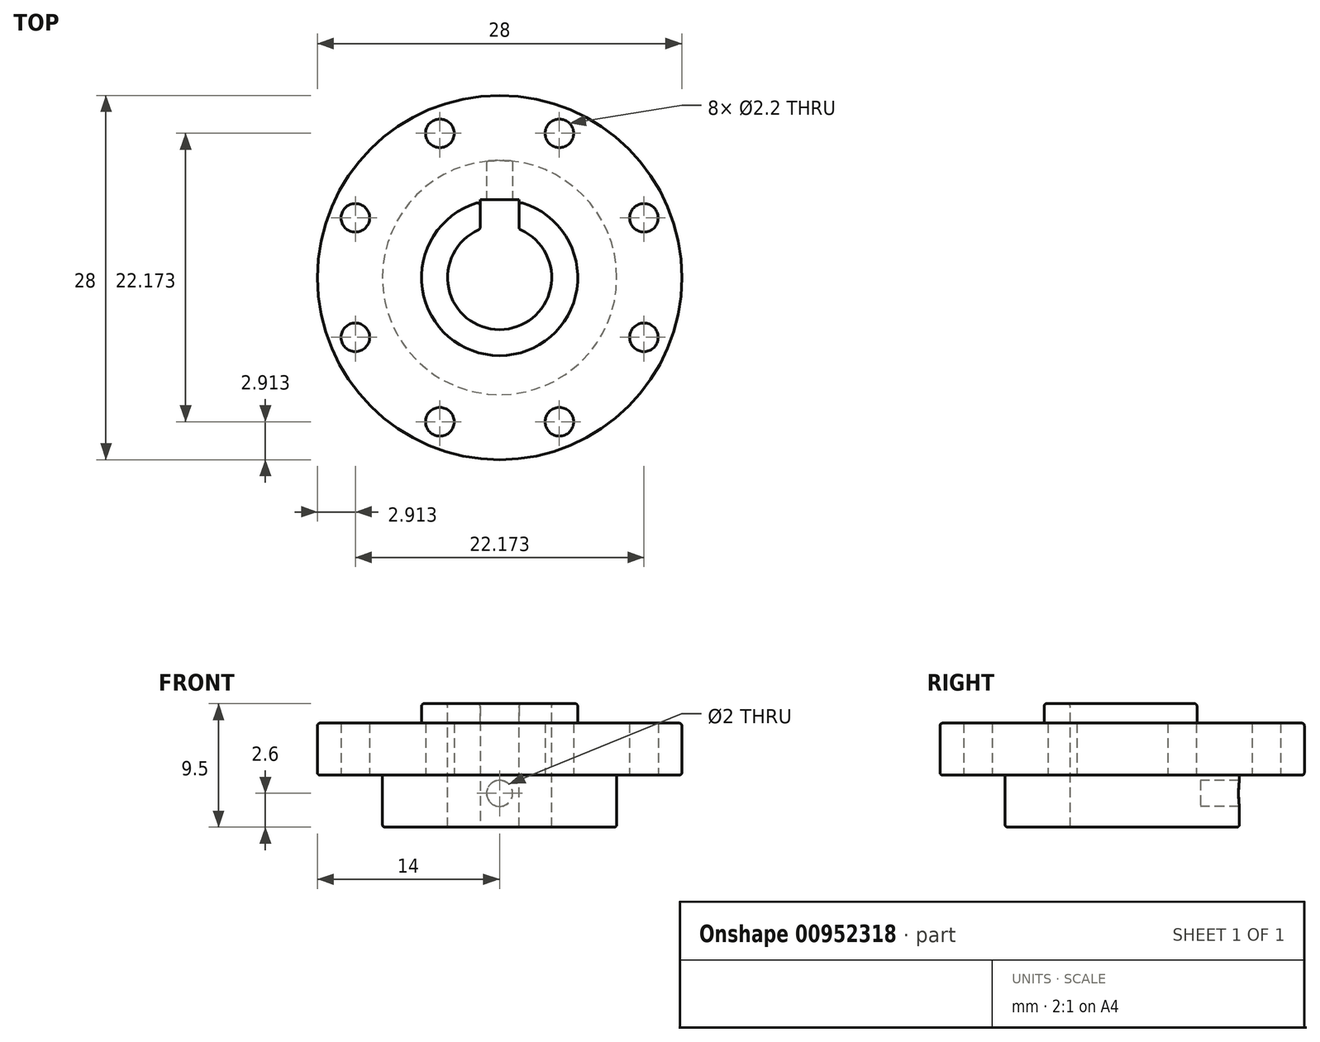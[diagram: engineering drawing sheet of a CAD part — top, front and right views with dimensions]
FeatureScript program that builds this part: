
annotation { "Feature Type Name" : "Feature", "Feature Type Description" : "" }
export const myFeature = defineFeature(function(context is Context, id is Id, definition is map)
    precondition{}
    {
        {
            var Q0;
            Q0=qCreatedBy(makeId("Top.planeOp"),FACE);
            var sketch = newSketch(context, id + "F0", { "sketchPlane" : qUnion([Q0])});
            skCircle(sketch, "E0", {"center": v(0, 0) * mm, "radius": 14 * mm});
            skSolve(sketch);
        }
        {
            var Q0;
            Q0 = qSketchRegion(id + "F0", true);
            extrude(context, id + "F1", {"entities" : qUnion([Q0]), "depth" : 4 * mm, "offsetDistance" : 25 * mm});
        }
        {
            var Q0;
            Q0=makeQuery(id+"F1.opExtrude","CAP_FACE",FACE,{"disambiguationData":[OSD([sQuery(id+"F0.wireOp",EDGE,"knUi2pX4-qsrH-ZYnk-r2x0-8cSF1UmVhSbS"),sQuery(id+"F0.wireOp",EDGE,"E0")])],"isStart":true});
            var sketch = newSketch(context, id + "F2", { "sketchPlane" : qUnion([Q0])});
            skCircle(sketch, "E1", {"center": v(0, 0) * mm, "radius": 9 * mm});
            skSolve(sketch);
        }
        {
            var Q0;
            Q0 = qSketchRegion(id + "F2", true);
            extrude(context, id + "F3", {"entities" : qUnion([Q0]), "operationType" : NewBodyOperationType.ADD, "depth" : 4 * mm, "offsetDistance" : 25 * mm});
        }
        {
            var Q0;
            Q0=makeQuery(id+"F1.opExtrude","CAP_FACE",FACE,{"disambiguationData":[OSD([sQuery(id+"F0.wireOp",EDGE,"E0")])],"isStart":false});
            var sketch = newSketch(context, id + "F4", { "sketchPlane" : qUnion([Q0])});
            skCircle(sketch, "E2", {"center": v(0, 0) * mm, "radius": 4 * mm});
            skSolve(sketch);
        }
        {
            var Q0;
            Q0 = qSketchRegion(id + "F4", true);
            var Q1;
            Q1=makeQuery(id+"F3.opExtrude","CAP_FACE",FACE,{"disambiguationData":[OSD([sQuery(id+"F2.wireOp",EDGE,"E1")])],"isStart":false});
            extrude(context, id + "F5", {"entities" : qUnion([Q0]), "operationType" : NewBodyOperationType.REMOVE, "endBound" : BoundingType.UP_TO_SURFACE, "oppositeDirection" : true, "depth" : 25 * mm, "endBoundEntityFace" : qUnion([Q1]), "offsetDistance" : 25 * mm});
        }
        {
            var Q0;
            Q0=makeQuery(id+"F1.opExtrude","CAP_FACE",FACE,{"disambiguationData":[OSD([sQuery(id+"F0.wireOp",EDGE,"E0")])],"isStart":true});
            var sketch = newSketch(context, id + "F6", { "sketchPlane" : qUnion([Q0])});
            skCircle(sketch, "E3", {"center": v(4.6, 11.09) * mm, "radius": 1.1 * mm});
            skCircle(sketch, "E4.1.0", {"center": v(-4.6, 11.09) * mm, "radius": 1.1 * mm});
            skCircle(sketch, "E4.2.0", {"center": v(-11.09, 4.6) * mm, "radius": 1.1 * mm});
            skCircle(sketch, "E4.3.0", {"center": v(-11.09, -4.6) * mm, "radius": 1.1 * mm});
            skCircle(sketch, "E4.4.0", {"center": v(-4.6, -11.09) * mm, "radius": 1.1 * mm});
            skCircle(sketch, "E4.5.0", {"center": v(4.6, -11.09) * mm, "radius": 1.1 * mm});
            skCircle(sketch, "E4.6.0", {"center": v(11.09, -4.6) * mm, "radius": 1.1 * mm});
            skCircle(sketch, "E4.7.0", {"center": v(11.09, 4.6) * mm, "radius": 1.1 * mm});
            skPoint(sketch, "E4.center", {"position": v(0, 0) * mm});
            skLineSegment(sketch, "E5", {"start": v(4.6, -11.09) * mm, "end": v(0, 0) * mm});
            skSolve(sketch);
        }
        {
            var Q0;
            Q0 = qSketchRegion(id + "F6", true);
            var Q1;
            Q1=makeQuery(id+"F1.opExtrude","CAP_FACE",FACE,{"disambiguationData":[OSD([sQuery(id+"F0.wireOp",EDGE,"E0")])],"isStart":false});
            extrude(context, id + "F7", {"entities" : qUnion([Q0]), "operationType" : NewBodyOperationType.REMOVE, "endBound" : BoundingType.UP_TO_SURFACE, "oppositeDirection" : true, "depth" : 25 * mm, "endBoundEntityFace" : qUnion([Q1]), "offsetDistance" : 25 * mm});
        }
        {
            var Q0;
            Q0=makeQuery(id+"F1.opExtrude","CAP_FACE",FACE,{"disambiguationData":[OSD([sQuery(id+"F0.wireOp",EDGE,"E0")])],"isStart":false});
            var sketch = newSketch(context, id + "F8", { "sketchPlane" : qUnion([Q0])});
            skLineSegment(sketch, "E6.bottom", {"start": v(1.5, 3) * mm, "end": v(-1.5, 3) * mm});
            skLineSegment(sketch, "E6.top", {"start": v(1.5, 6) * mm, "end": v(-1.5, 6) * mm});
            skLineSegment(sketch, "E6.left", {"start": v(1.5, 3) * mm, "end": v(1.5, 6) * mm});
            skLineSegment(sketch, "E6.right", {"start": v(-1.5, 3) * mm, "end": v(-1.5, 6) * mm});
            skPoint(sketch, "E6.middle", {"position": v(0, 4.5) * mm});
            skSolve(sketch);
        }
        {
            var Q0;
            {var subQ0=sQuery(id+"F8.wireOp",EDGE,"E6.top");Q0=makeQuery(id+"F8.imprint","IMPRINT",FACE,{"disambiguationData":[TD([[makeQuery(id+"F8.imprint","IMPRINT",EDGE,{"derivedFrom":subQ0}),1.0]])]});}
            var Q1;
            Q1=makeQuery(id+"F3.opExtrude","CAP_FACE",FACE,{"disambiguationData":[OSD([sQuery(id+"F2.wireOp",EDGE,"E1")])],"isStart":false});
            extrude(context, id + "F9", {"entities" : qUnion([Q0]), "operationType" : NewBodyOperationType.REMOVE, "endBound" : BoundingType.UP_TO_SURFACE, "oppositeDirection" : true, "depth" : 25 * mm, "endBoundEntityFace" : qUnion([Q1]), "offsetDistance" : 25 * mm});
        }
        {
            var Q0;
            Q0=qCreatedBy(makeId("Front.planeOp"),FACE);
            var sketch = newSketch(context, id + "F10", { "sketchPlane" : qUnion([Q0])});
            skCircle(sketch, "E7", {"center": v(0, -1.4) * mm, "radius": 1 * mm});
            skSolve(sketch);
        }
        {
            var Q0;
            Q0 = qSketchRegion(id + "F10", true);
            extrude(context, id + "F11", {"entities" : qUnion([Q0]), "operationType" : NewBodyOperationType.REMOVE, "oppositeDirection" : true, "depth" : 25 * mm, "offsetDistance" : 25 * mm});
        }
        {
            var Q0;
            Q0=makeQuery(id+"F1.opExtrude","CAP_FACE",FACE,{"disambiguationData":[OSD([sQuery(id+"F0.wireOp",EDGE,"E0")])],"isStart":false});
            var sketch = newSketch(context, id + "F12", { "sketchPlane" : qUnion([Q0])});
            skCircle(sketch, "E8", {"center": v(0, 0) * mm, "radius": 6 * mm});
            skCircle(sketch, "E9", {"center": v(0, 0) * mm, "radius": 4 * mm});
            skLineSegment(sketch, "E10", {"start": v(-1.5, 3.7) * mm, "end": v(-1.5, 5.8) * mm});
            skLineSegment(sketch, "E11", {"start": v(1.5, 3.7) * mm, "end": v(1.5, 5.8) * mm});
            skSolve(sketch);
        }
        {
            var Q0;
            {var subQ0=sQuery(id+"F12.wireOp",EDGE,"E10");Q0=makeQuery(id+"F12.imprint","IMPRINT",FACE,{"disambiguationData":[TD([[makeQuery(id+"F12.imprint","IMPRINT",EDGE,{"derivedFrom":subQ0}),1.0]])]});}
            extrude(context, id + "F13", {"entities" : qUnion([Q0]), "operationType" : NewBodyOperationType.ADD, "depth" : 1.5 * mm, "offsetDistance" : 25 * mm});
        }
        {
            var Q0;
            Q0=makeQuery(id+"F1.opExtrude","CAP_EDGE",EDGE,{"disambiguationData":[OSD([sQuery(id+"F0.wireOp",EDGE,"E0")])],"isStart":false});
            var Q1;
            Q1=makeQuery(id+"F1.opExtrude","CAP_EDGE",EDGE,{"disambiguationData":[OSD([sQuery(id+"F0.wireOp",EDGE,"E0")])],"isStart":true});
            var Q2;
            Q2=makeQuery(id+"F3.opExtrude","CAP_EDGE",EDGE,{"disambiguationData":[OSD([sQuery(id+"F2.wireOp",EDGE,"E1")])],"isStart":false});
            var Q3;
            Q3=makeQuery(id+"F5.boolean.opBoolean","COPY",EDGE,{"derivedFrom":makeQuery(id+"F5.opExtrude","CAP_EDGE",EDGE,{"disambiguationData":[OSD([sQuery(id+"F4.wireOp",EDGE,"E2")])],"isStart":false})});
            var Q4;
            Q4=makeQuery(id+"F13.opExtrude","CAP_FACE",FACE,{"disambiguationData":[OSD([sQuery(id+"F12.wireOp",EDGE,"E8"),sQuery(id+"F12.wireOp",EDGE,"E9"),sQuery(id+"F12.wireOp",EDGE,"E10"),sQuery(id+"F12.wireOp",EDGE,"E11")])],"isStart":false});
            var Q5;
            Q5=makeQuery(id+"F9.boolean.opBoolean","COPY",EDGE,{"derivedFrom":makeQuery(id+"F9.opExtrude","CAP_EDGE",EDGE,{"disambiguationData":[OSD([sQuery(id+"F8.wireOp",EDGE,"E6.left")])],"isStart":true})});
            var Q6;
            Q6=makeQuery(id+"F9.boolean.opBoolean","COPY",EDGE,{"derivedFrom":makeQuery(id+"F9.opExtrude","CAP_EDGE",EDGE,{"disambiguationData":[OSD([sQuery(id+"F8.wireOp",EDGE,"E6.top")])],"isStart":true})});
            var Q7;
            Q7=makeQuery(id+"F9.boolean.opBoolean","COPY",EDGE,{"derivedFrom":makeQuery(id+"F9.opExtrude","CAP_EDGE",EDGE,{"disambiguationData":[OSD([sQuery(id+"F8.wireOp",EDGE,"E6.right")])],"isStart":true})});
            var Q8;
            Q8=makeQuery(id+"F13.opExtrude","SWEPT_EDGE",EDGE,{"disambiguationData":[OSD([sQuery(id+"F8.wireOp",EDGE,"E6.left"),sQuery(id+"F12.wireOp",EDGE,"E8"),sQuery(id+"F12.wireOp",EDGE,"E11")])]});
            var Q9;
            Q9=makeQuery(id+"F13.opExtrude","SWEPT_EDGE",EDGE,{"disambiguationData":[OSD([sQuery(id+"F8.wireOp",EDGE,"E6.right"),sQuery(id+"F12.wireOp",EDGE,"E8"),sQuery(id+"F12.wireOp",EDGE,"E10")])]});
            var Q10;
            Q10=makeQuery(id+"F13.boolean.opBoolean","MERGE",EDGE,{"derivedFrom":[makeQuery(id+"F9.boolean.opBoolean","COPY",EDGE,{"derivedFrom":makeQuery(id+"F9.opExtrude","SWEPT_EDGE",EDGE,{"disambiguationData":[OSD([sQuery(id+"F4.wireOp",EDGE,"E2"),sQuery(id+"F8.wireOp",EDGE,"E6.right")])]})}),makeQuery(id+"F13.opExtrude","SWEPT_EDGE",EDGE,{"disambiguationData":[OSD([sQuery(id+"F12.wireOp",EDGE,"E9"),sQuery(id+"F12.wireOp",EDGE,"E10")])]})]});
            var Q11;
            Q11=makeQuery(id+"F13.boolean.opBoolean","MERGE",EDGE,{"derivedFrom":[makeQuery(id+"F9.boolean.opBoolean","COPY",EDGE,{"derivedFrom":makeQuery(id+"F9.opExtrude","SWEPT_EDGE",EDGE,{"disambiguationData":[OSD([sQuery(id+"F4.wireOp",EDGE,"E2"),sQuery(id+"F8.wireOp",EDGE,"E6.left")])]})}),makeQuery(id+"F13.opExtrude","SWEPT_EDGE",EDGE,{"disambiguationData":[OSD([sQuery(id+"F12.wireOp",EDGE,"E9"),sQuery(id+"F12.wireOp",EDGE,"E11")])]})]});
            var Q12;
            Q12=makeQuery(id+"F9.boolean.opBoolean","COPY",EDGE,{"derivedFrom":makeQuery(id+"F9.opExtrude","CAP_EDGE",EDGE,{"disambiguationData":[OSD([sQuery(id+"F8.wireOp",EDGE,"E6.left")])],"isStart":false})});
            var Q13;
            Q13=makeQuery(id+"F9.boolean.opBoolean","COPY",EDGE,{"derivedFrom":makeQuery(id+"F9.opExtrude","CAP_EDGE",EDGE,{"disambiguationData":[OSD([sQuery(id+"F8.wireOp",EDGE,"E6.top")])],"isStart":false})});
            var Q14;
            Q14=makeQuery(id+"F9.boolean.opBoolean","COPY",EDGE,{"derivedFrom":makeQuery(id+"F9.opExtrude","CAP_EDGE",EDGE,{"disambiguationData":[OSD([sQuery(id+"F8.wireOp",EDGE,"E6.right")])],"isStart":false})});
            fillet(context, id + "F14", {"entities" : qUnion([Q0, Q1, Q2, Q3, Q4, Q5, Q6, Q7, Q8, Q9, Q10, Q11, Q12, Q13, Q14]), "radius" : 0.2 * mm, "tangentPropagation" : true, "allowEdgeOverflow" : false});
        }
    });
